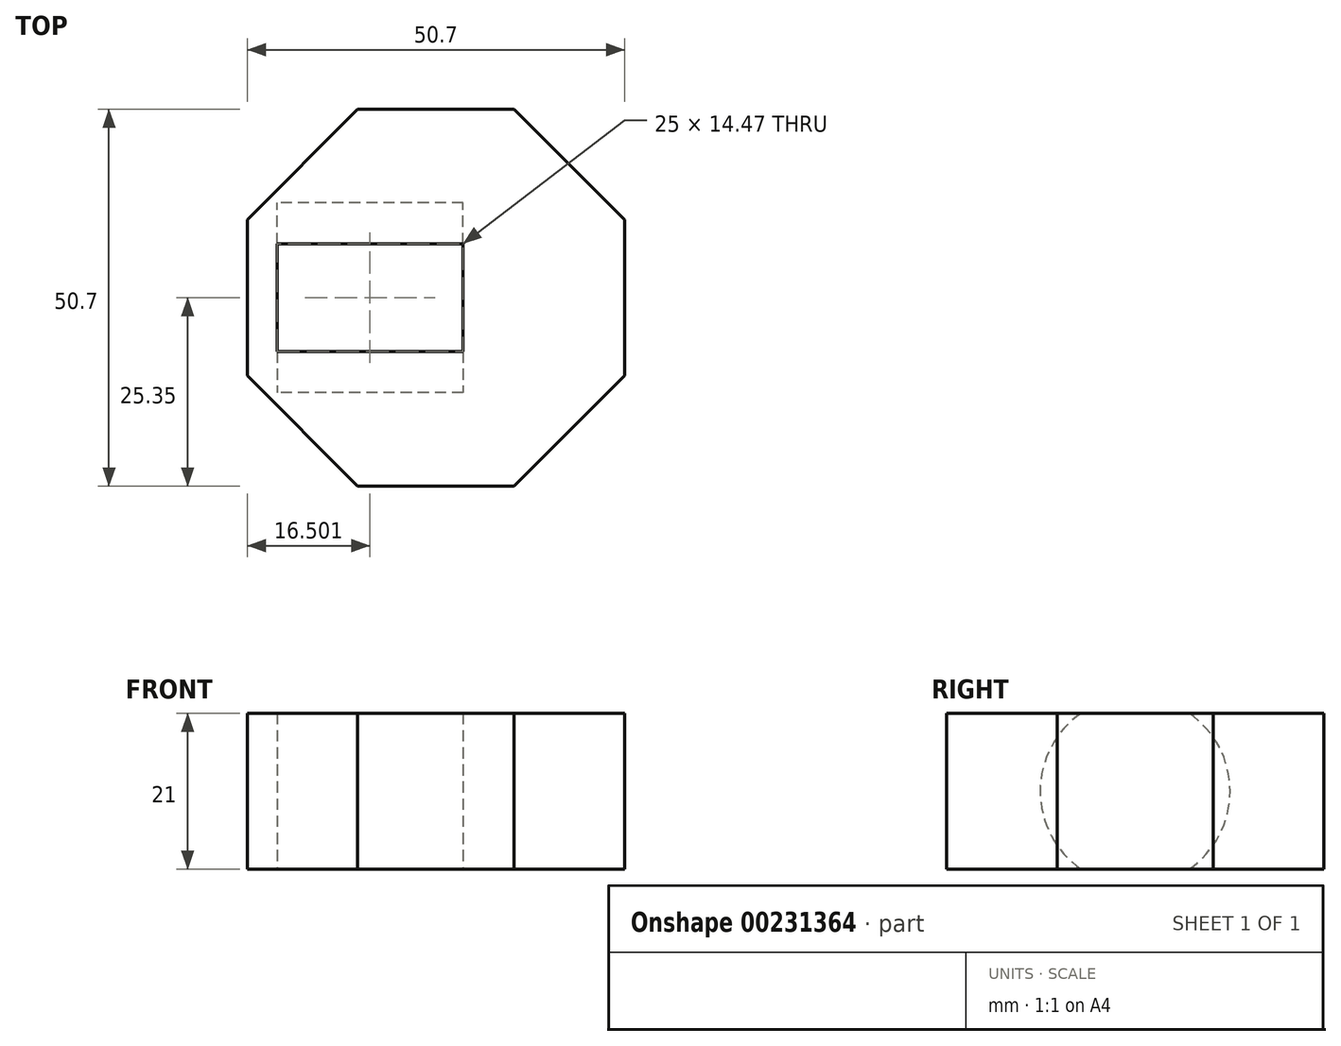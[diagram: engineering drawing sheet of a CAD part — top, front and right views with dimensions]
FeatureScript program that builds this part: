
annotation { "Feature Type Name" : "Feature", "Feature Type Description" : "" }
export const myFeature = defineFeature(function(context is Context, id is Id, definition is map)
    precondition{}
    {
        {
            var Q0;
            Q0=qCreatedBy(makeId("Top.planeOp"),FACE);
            var sketch = newSketch(context, id + "F0", { "sketchPlane" : qUnion([Q0])});
            skCircle(sketch, "E0.cCircle", {"center": v(0, 0) * mm, "radius": 25.35 * mm, "construction": true});
            skLineSegment(sketch, "E0.0", {"start": v(25.35, 10.5) * mm, "end": v(25.35, -10.5) * mm});
            skLineSegment(sketch, "E0.1", {"start": v(25.35, -10.5) * mm, "end": v(10.5, -25.35) * mm});
            skLineSegment(sketch, "E0.2", {"start": v(10.5, -25.35) * mm, "end": v(-10.5, -25.35) * mm});
            skLineSegment(sketch, "E0.3", {"start": v(-10.5, -25.35) * mm, "end": v(-25.35, -10.5) * mm});
            skLineSegment(sketch, "E0.4", {"start": v(-25.35, -10.5) * mm, "end": v(-25.35, 10.5) * mm});
            skLineSegment(sketch, "E0.5", {"start": v(-25.35, 10.5) * mm, "end": v(-10.5, 25.35) * mm});
            skLineSegment(sketch, "E0.6", {"start": v(-10.5, 25.35) * mm, "end": v(10.5, 25.35) * mm});
            skLineSegment(sketch, "E0.7", {"start": v(10.5, 25.35) * mm, "end": v(25.35, 10.5) * mm});
            skPoint(sketch, "E0.0.midPoint", {"position": v(25.35, 0) * mm});
            skLineSegment(sketch, "E1.bottom", {"start": v(-12.5, 12.5) * mm, "end": v(12.5, 12.5) * mm});
            skLineSegment(sketch, "E1.top", {"start": v(-12.5, -12.5) * mm, "end": v(12.5, -12.5) * mm});
            skLineSegment(sketch, "E1.left", {"start": v(-12.5, 12.5) * mm, "end": v(-12.5, -12.5) * mm});
            skLineSegment(sketch, "E1.right", {"start": v(12.5, 12.5) * mm, "end": v(12.5, -12.5) * mm});
            skSolve(sketch);
        }
        {
            var Q0;
            Q0 = qSketchRegion(id + "F0", true);
            var Q1;
            Q1=makeQuery(id+"F0.imprint","IMPRINT",FACE,{"disambiguationData":[TD([[makeQuery(id+"F0.imprint","IMPRINT",EDGE,{"derivedFrom":sQuery(id+"F0.wireOp",EDGE,"E1.bottom")}),-1.0]])]});
            extrude(context, id + "F1", {"entities" : qUnion([Q0, Q1]), "depth" : 21 * mm});
        }
        {
            var Q0;
            Q0=makeQuery(id+"F1.opExtrude","SWEPT_FACE",FACE,{"disambiguationData":[OSD([sQuery(id+"F0.wireOp",EDGE,"E0.4")])]});
            var sketch = newSketch(context, id + "F2", { "sketchPlane" : qUnion([Q0])});
            skLineSegment(sketch, "E2", {"start": v(-10.5, 10.5) * mm, "end": v(10.5, 10.5) * mm});
            skCircle(sketch, "E3", {"center": v(0, 10.5) * mm, "radius": 12.75 * mm});
            skSolve(sketch);
        }
        {
            var Q0;
            Q0 = qSketchRegion(id + "F2", true);
            extrude(context, id + "F3", {"entities" : qUnion([Q0]), "operationType" : NewBodyOperationType.REMOVE, "oppositeDirection" : true, "depth" : 29 * mm, "hasSecondDirection" : true, "secondDirectionOppositeDirection" : true, "secondDirectionDepth" : 4 * mm});
        }
    });
